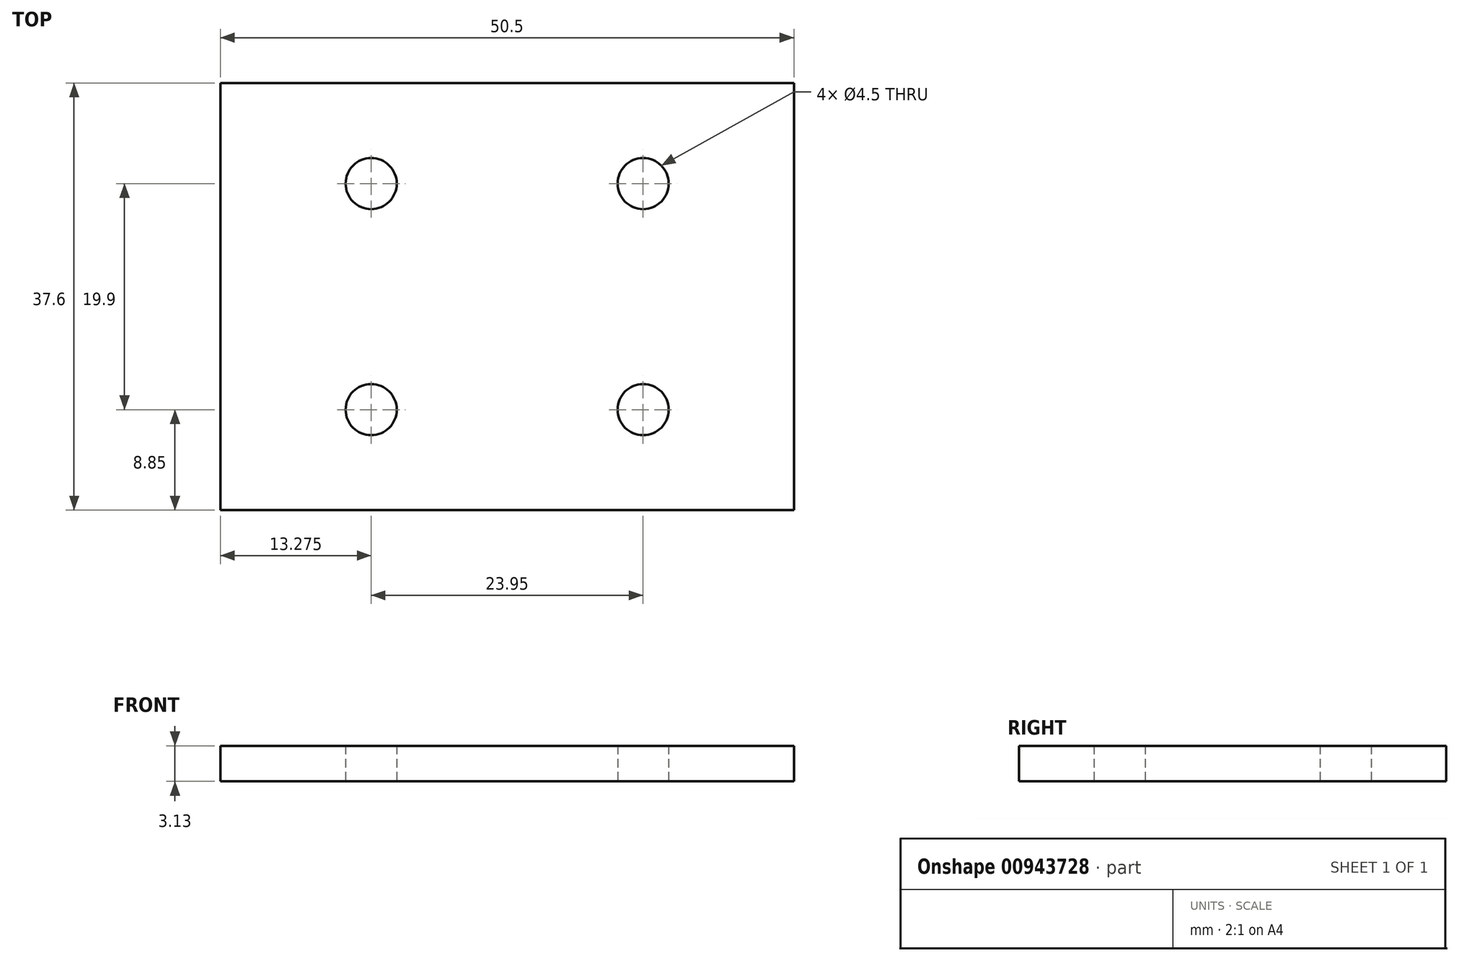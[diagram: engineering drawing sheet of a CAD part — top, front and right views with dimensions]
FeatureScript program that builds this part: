
annotation { "Feature Type Name" : "Feature", "Feature Type Description" : "" }
export const myFeature = defineFeature(function(context is Context, id is Id, definition is map)
    precondition{}
    {
        {
            var Q0;
            Q0=qCreatedBy(makeId("Top.planeOp"),FACE);
            var sketch = newSketch(context, id + "F0", { "sketchPlane" : qUnion([Q0])});
            skLineSegment(sketch, "E0.bottom", {"start": v(25.25, 18.8) * mm, "end": v(-25.25, 18.8) * mm});
            skLineSegment(sketch, "E0.top", {"start": v(25.25, -18.8) * mm, "end": v(-25.25, -18.8) * mm});
            skLineSegment(sketch, "E0.left", {"start": v(25.25, 18.8) * mm, "end": v(25.25, -18.8) * mm});
            skLineSegment(sketch, "E0.right", {"start": v(-25.25, 18.8) * mm, "end": v(-25.25, -18.8) * mm});
            skPoint(sketch, "E0.middle", {"position": v(0, 0) * mm});
            skLineSegment(sketch, "E1.bottom", {"start": v(11.98, 9.95) * mm, "end": v(-11.98, 9.95) * mm, "construction": true});
            skLineSegment(sketch, "E1.top", {"start": v(11.98, -9.95) * mm, "end": v(-11.98, -9.95) * mm, "construction": true});
            skLineSegment(sketch, "E1.left", {"start": v(11.98, 9.95) * mm, "end": v(11.98, -9.95) * mm, "construction": true});
            skLineSegment(sketch, "E1.right", {"start": v(-11.98, 9.95) * mm, "end": v(-11.98, -9.95) * mm, "construction": true});
            skCircle(sketch, "E2", {"center": v(11.98, 9.95) * mm, "radius": 2.25 * mm});
            skCircle(sketch, "E3", {"center": v(-11.98, 9.95) * mm, "radius": 2.25 * mm});
            skCircle(sketch, "E4", {"center": v(-11.98, -9.95) * mm, "radius": 2.25 * mm});
            skCircle(sketch, "E5", {"center": v(11.98, -9.95) * mm, "radius": 2.25 * mm});
            skSolve(sketch);
        }
        {
            var Q0;
            Q0 = qSketchRegion(id + "F0", true);
            extrude(context, id + "F1", {"entities" : qUnion([Q0]), "depth" : 3.13 * mm, "offsetDistance" : 25 * mm});
        }
    });
